# Revit family: SYSIMPLE FDT27A
name_source: partatom
category: Оборудование
units: mm (PartAtom-declared; Revit-internal decimal feet)

## family parameters
Всегда вертикально = Да
На основе рабочей плоскости = Нет
Общий = Нет
При загрузке вырезать с полостями = Нет
Размер круглого соединителя = Использовать диаметр
Тип детали = Нормальный
Точка расчета площади = Нет

## types (1)
- SYSIMPLE FDT27A
    Air guide size(mm) = /
    Body dimension(mm) = 894×518×240
    COP = /
    Capacity = /
    Chassis height（mm) = /
    Compressor quantity = /
    Compressor type = /
    Cooling Power input = /
    Cooling capacity = 2700/2305/1763
    Cooling current = /
    Current of Circuit breaker = /
    Drain Pipe (mm) = DN20
    EER = /
    Fan motor quantity = 1
    Front clearance(mm) = /
    Heating capacity = 4050/3460/2646
    Heating current = /
    Heating power input = /
    Hydraulic Resistance = 30
    Inlet/Outlet Water Pipe (mm) = DN20
    Installation hole spacing（D) = /
    Installation hole spacing（W) = /
    Left Side clearance(ODU side mm) = /
    Left Side clearance(wall side mm) = /
    Manufacturer URL = /
    Max.Current input = /
    Max.Power input = /
    Max.Working pressure = 1.6
    Model = AFC-300HCR/4BA6
    Noise Level(dB) = ≤42
    Operation range Heatling (°C） = /
    Operation range cooling (°C） = /
    Power = 220~240V,50Hz,1
    Product series = FCU-Horizontal duct 6 series 50HZ
    Protection grade = /
    Rear clearance(mm) = /
    Right Side clearance(ODU side mm) = /
    Right Side clearance(wall side mm) = /
    Static pressure（pa） = 30
    Water Flow Volume = 0.61
    Weight(G) = 18.9
    Weight(N) = 16.4
    fan type = Low noise 3-speed fan motor         ( PG13A )
    Изготовитель = AUX
